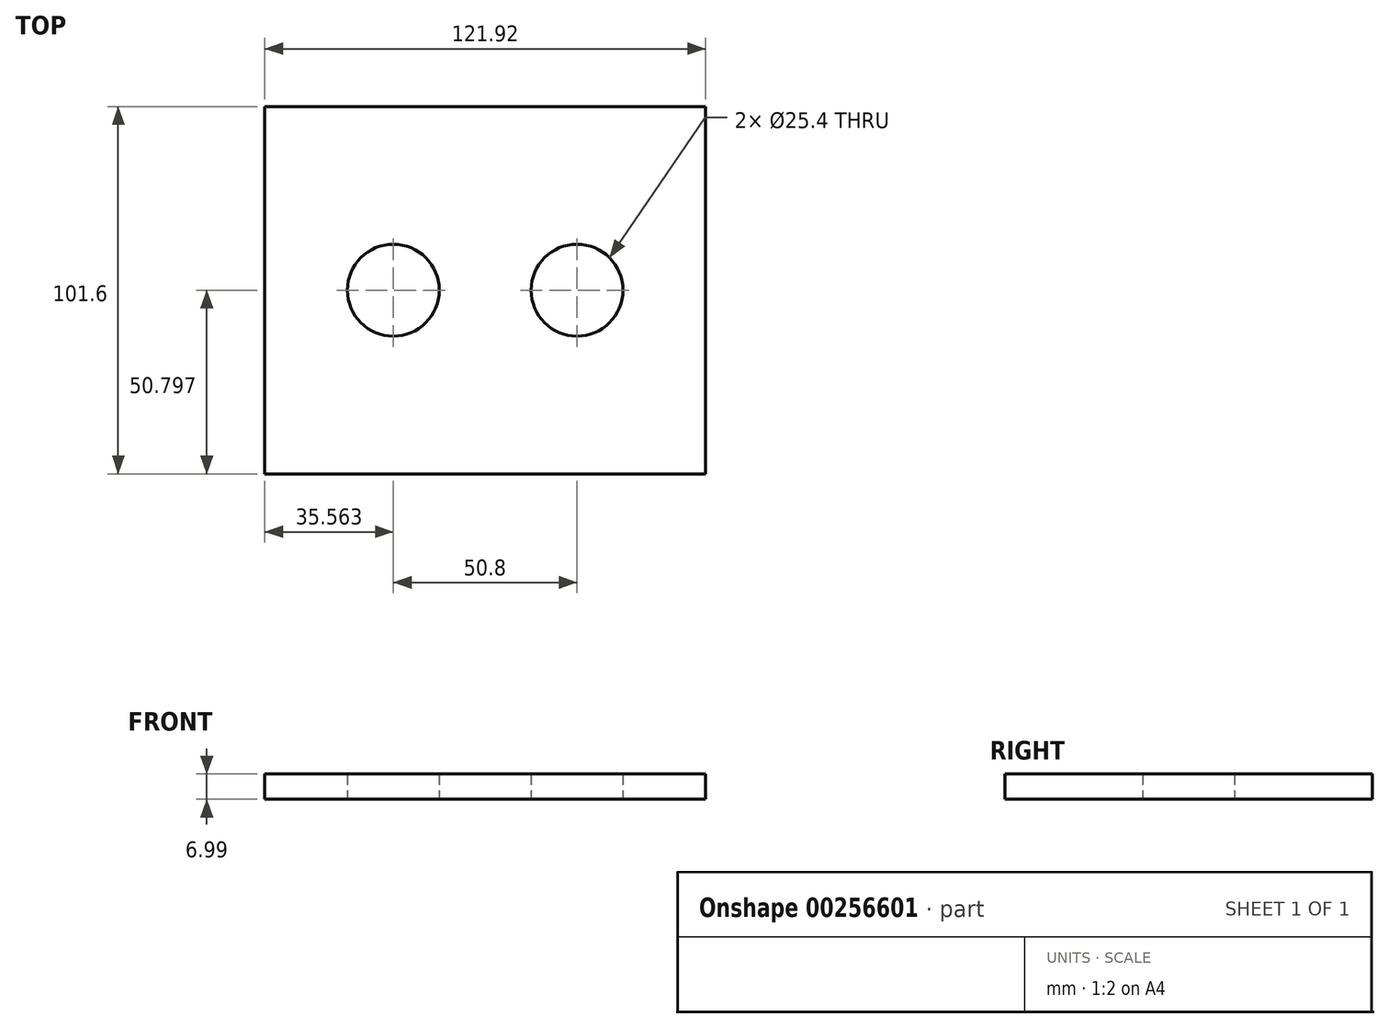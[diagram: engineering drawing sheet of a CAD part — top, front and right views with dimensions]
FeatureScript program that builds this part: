
annotation { "Feature Type Name" : "Feature", "Feature Type Description" : "" }
export const myFeature = defineFeature(function(context is Context, id is Id, definition is map)
    precondition{}
    {
        {
            var Q0;
            Q0=qCreatedBy(makeId("Top.planeOp"),FACE);
            var sketch = newSketch(context, id + "F0", { "sketchPlane" : qUnion([Q0])});
            skLineSegment(sketch, "E0.bottom", {"start": v(-63.12, 69.1) * mm, "end": v(58.8, 69.1) * mm});
            skLineSegment(sketch, "E0.top", {"start": v(-63.12, -32.5) * mm, "end": v(58.8, -32.5) * mm});
            skLineSegment(sketch, "E0.left", {"start": v(-63.12, 69.1) * mm, "end": v(-63.12, -32.5) * mm});
            skLineSegment(sketch, "E0.right", {"start": v(58.8, 69.1) * mm, "end": v(58.8, -32.5) * mm});
            skCircle(sketch, "E1", {"center": v(-27.56, 18.3) * mm, "radius": 12.7 * mm});
            skCircle(sketch, "E2", {"center": v(23.24, 18.3) * mm, "radius": 12.7 * mm});
            skSolve(sketch);
        }
        {
            var Q0;
            Q0 = qSketchRegion(id + "F0", true);
            extrude(context, id + "F1", {"entities" : qUnion([Q0]), "depth" : 7 * mm});
        }
    });
